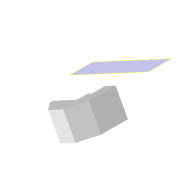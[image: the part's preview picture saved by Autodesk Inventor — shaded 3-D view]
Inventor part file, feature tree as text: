
AUTODESK INVENTOR PART (.ipt)
format: ipt  version: 2022 (Build 260153000, 153)  size: 225,792 bytes
history: native  units: in
note: dims shown in document units (in); Inventor stores cm internally (conversion verified against a paired STEP export)
features: extrude x6, other x6, sketch x5, reference x4, projected_geometry x2, plane x1
ambient origin geometry x8: Origin, YZ Plane, XZ Plane, XY Plane, X Axis, Y Axis, Z Axis, Center Point
bodies: Solid1 (feature_tree)
feature tree (24):
  plane  "Work Plane1"
  extrude  "Extrusion1"  Depth=0.5512in TaperAngle=0.0deg
  extrude  "Extrusion2"  Depth=0.0591in
  extrude  "Extrusion3"  TaperAngle=135.0deg  [1 undecoded]
  extrude  "Extrusion8"  Depth=0.2362in
  extrude  "Extrusion9"  Depth=0.5512in
  extrude  "Extrusion11"  Depth=0.3937in
  sketch  "Sketch2"  dims[d0=0.0591in d1=0.0in d3=0.5512in d4=0.0in]
  sketch  "Sketch3"  dims[d12=0.0591in d13=0.0in d22=0.5307in]
  reference  "Reference1"
  projected_geometry  "Projected Loop5"
  projected_geometry  "Projected Loop6"
  sketch  "Sketch8"  dims[d23=0.2653in d25=135.0deg]
  reference  "Reference2"
  reference  "Reference3"
  sketch  "Sketch9"  dims[d26=0.1575in d27=0.2362in]
  reference  "Reference4"
  sketch  "Skizze11"  dims[d28=0.1568in d29=0.2362in d31=0.3937in d35=0.5512in d36=0.0in d40=0.0591in d41=0.0591in d42=0.9449in d43=0.5512in d44=0.0in d45=0.0in d48=0.0in d49=0.0in]
  other  "<userpath>\Documents\Matchboxscope\INVENTOR\Matchboxscope_v0.iam"
  other  "Matchboxscope_v0.iam"
  other  "Matchboxscope_sample_v0:1"
  other  "Matchboxscope_middle2_v1:1"
  other  "00_ESP3-CAM:5"
  other  "Bauteil50"
note: 1 required parameter value undecoded (feature->parameter linkage not recoverable at this tier; creation-order binding heuristic only, values carry confidence <= 0.55)
